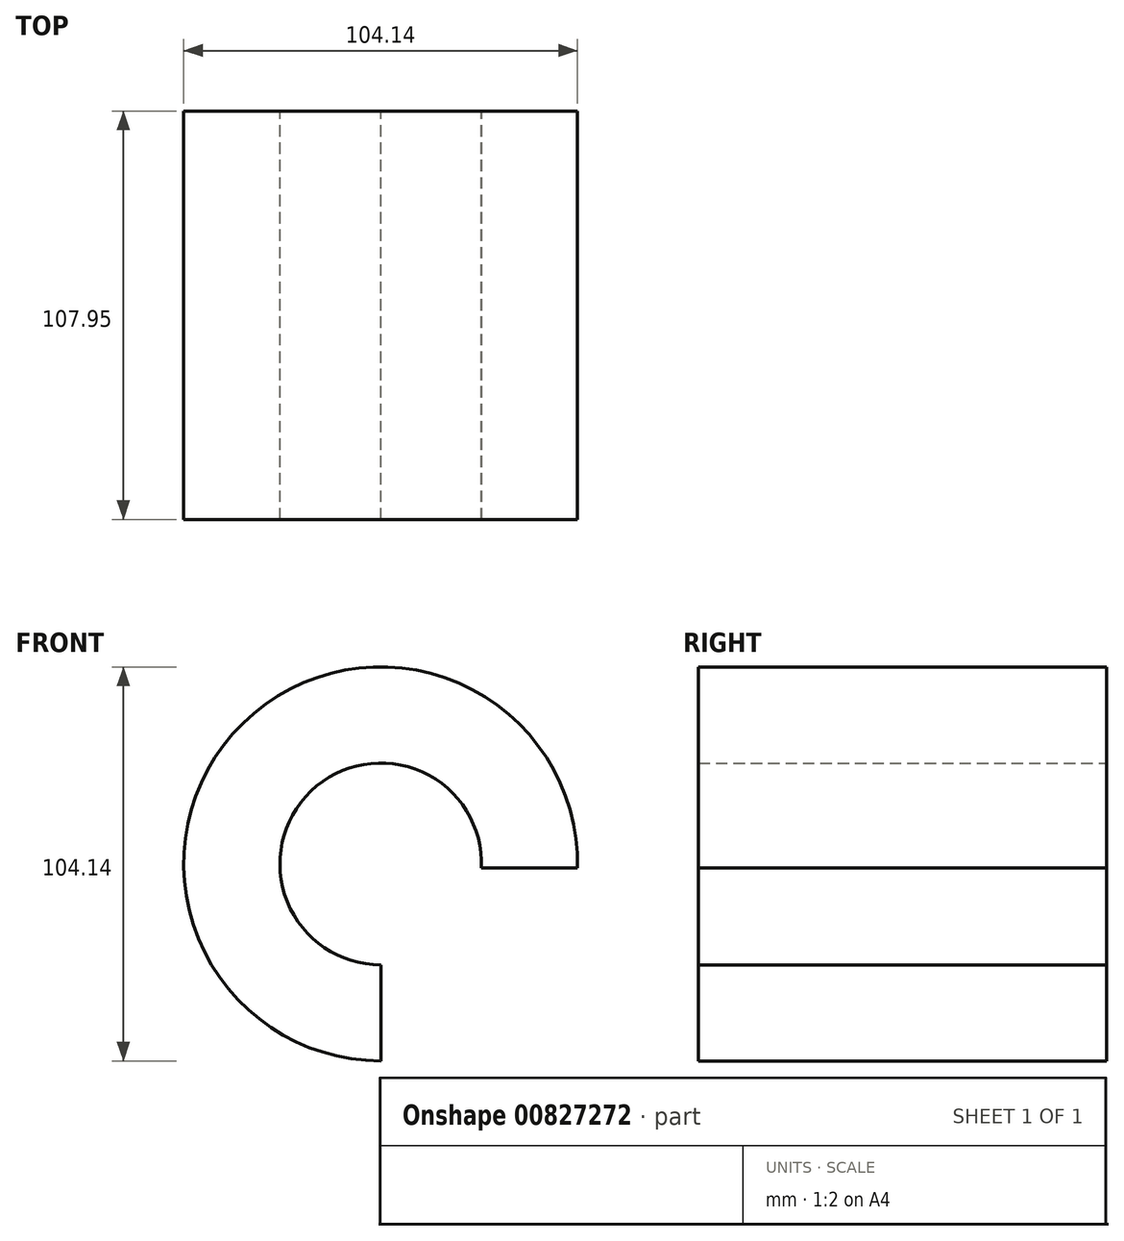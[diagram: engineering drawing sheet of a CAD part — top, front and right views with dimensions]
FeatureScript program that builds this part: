
annotation { "Feature Type Name" : "Feature", "Feature Type Description" : "" }
export const myFeature = defineFeature(function(context is Context, id is Id, definition is map)
    precondition{}
    {
        {
            var Q0;
            Q0=qCreatedBy(makeId("Front.planeOp"),FACE);
            var sketch = newSketch(context, id + "F0", { "sketchPlane" : qUnion([Q0])});
            skArc(sketch, "E0", {"start": v(0, 0) * mm, "mid": v(-18.47, 45.91) * mm, "end": v(26.65, 25.57) * mm});
            skLineSegment(sketch, "E1", {"start": v(0, 0) * mm, "end": v(0, -25.4) * mm});
            skLineSegment(sketch, "E2", {"start": v(26.65, 25.57) * mm, "end": v(52.05, 25.57) * mm});
            skArc(sketch, "E3", {"start": v(52.05, 25.57) * mm, "mid": v(-36.44, 63.87) * mm, "end": v(0, -25.4) * mm});
            skSolve(sketch);
        }
        {
            var Q0;
            Q0 = qSketchRegion(id + "F0", true);
            var Q1;
            Q1=makeQuery(id+"F0.imprint","IMPRINT",FACE,{"disambiguationData":[TD([[makeQuery(id+"F0.imprint","IMPRINT",EDGE,{"derivedFrom":sQuery(id+"F0.wireOp",EDGE,"E0")}),1.0]])]});
            extrude(context, id + "F1", {"entities" : qUnion([Q0, Q1]), "depth" : 107.95 * mm, "offsetDistance" : 25.4 * mm});
        }
    });
